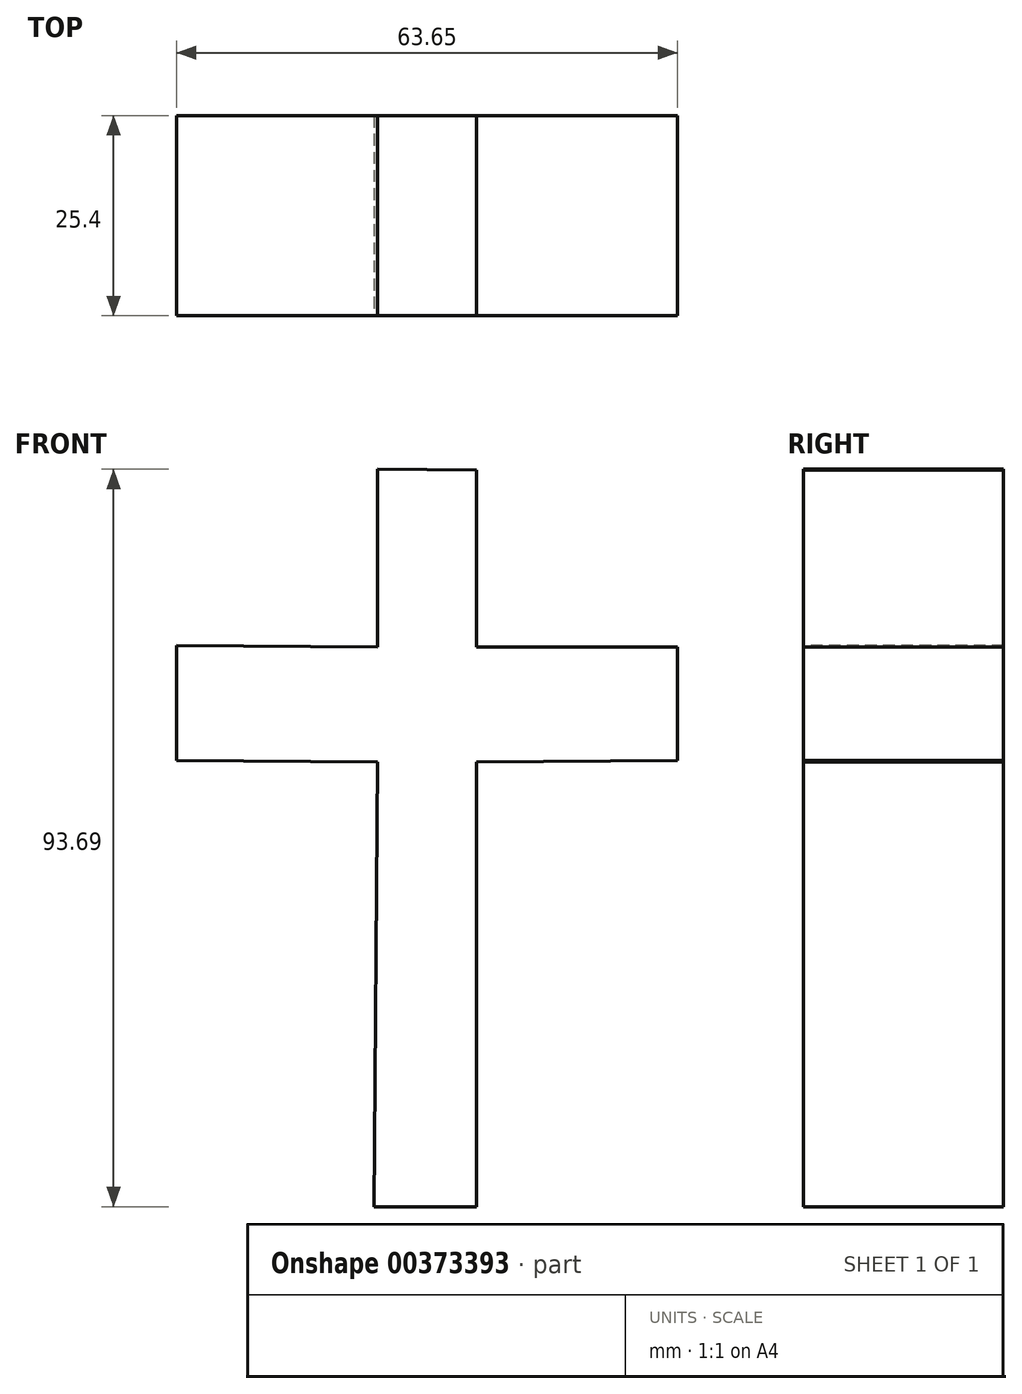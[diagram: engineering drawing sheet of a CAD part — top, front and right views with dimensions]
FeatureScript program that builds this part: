
annotation { "Feature Type Name" : "Feature", "Feature Type Description" : "" }
export const myFeature = defineFeature(function(context is Context, id is Id, definition is map)
    precondition{}
    {
        {
            var Q0;
            Q0=qCreatedBy(makeId("Front.planeOp"),FACE);
            var sketch = newSketch(context, id + "F0", { "sketchPlane" : qUnion([Q0])});
            skLineSegment(sketch, "E0", {"start": v(-6.72, -66.12) * mm, "end": v(6.28, -66.12) * mm});
            skLineSegment(sketch, "E1", {"start": v(6.28, -9.64) * mm, "end": v(6.28, -66.12) * mm});
            skLineSegment(sketch, "E2", {"start": v(-6.28, -9.64) * mm, "end": v(-6.72, -66.12) * mm});
            skLineSegment(sketch, "E3", {"start": v(-6.28, -9.64) * mm, "end": v(-31.82, -9.43) * mm});
            skLineSegment(sketch, "E4", {"start": v(-31.82, 5.15) * mm, "end": v(-31.82, -9.43) * mm});
            skLineSegment(sketch, "E5", {"start": v(-31.82, 5.15) * mm, "end": v(-6.28, 4.95) * mm});
            skLineSegment(sketch, "E6", {"start": v(-6.28, 4.95) * mm, "end": v(-6.28, 27.57) * mm});
            skLineSegment(sketch, "E7", {"start": v(-6.28, 27.57) * mm, "end": v(6.28, 27.47) * mm});
            skLineSegment(sketch, "E8", {"start": v(6.28, 27.47) * mm, "end": v(6.28, 4.95) * mm});
            skLineSegment(sketch, "E9", {"start": v(31.83, 4.95) * mm, "end": v(6.28, 4.95) * mm});
            skLineSegment(sketch, "E10", {"start": v(31.83, 4.95) * mm, "end": v(31.83, -9.43) * mm});
            skLineSegment(sketch, "E11", {"start": v(6.28, -9.64) * mm, "end": v(31.83, -9.43) * mm});
            skSolve(sketch);
        }
        {
            var Q0;
            Q0=makeQuery(id+"F0.imprint","IMPRINT",FACE,{"disambiguationData":[TD([[makeQuery(id+"F0.imprint","IMPRINT",EDGE,{"derivedFrom":sQuery(id+"F0.wireOp",EDGE,"E0")}),1.0]])]});
            extrude(context, id + "F1", {"entities" : qUnion([Q0]), "oppositeDirection" : true, "depth" : 25.4 * mm});
        }
    });
